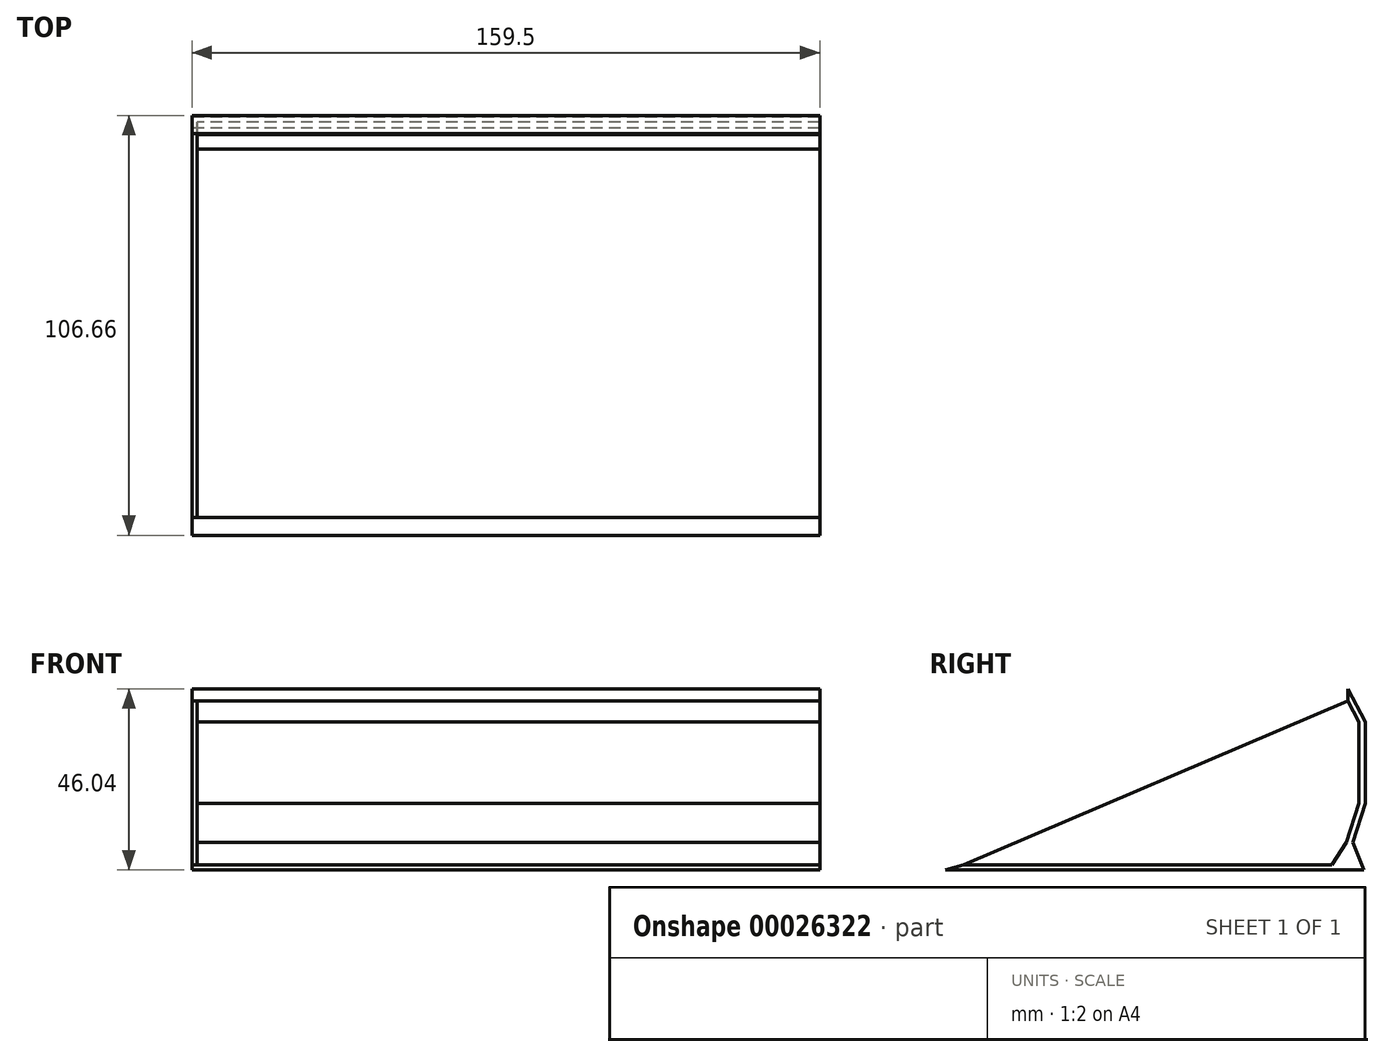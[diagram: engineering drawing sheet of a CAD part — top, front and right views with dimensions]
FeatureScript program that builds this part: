
annotation { "Feature Type Name" : "Feature", "Feature Type Description" : "" }
export const myFeature = defineFeature(function(context is Context, id is Id, definition is map)
    precondition{}
    {
        {
            var Q0;
            Q0=qCreatedBy(makeId("Right.planeOp"),FACE);
            var sketch = newSketch(context, id + "F0", { "sketchPlane" : qUnion([Q0])});
            skLineSegment(sketch, "E0", {"start": v(-60.67, 0) * mm, "end": v(38.43, 0) * mm});
            skLineSegment(sketch, "E1", {"start": v(38.43, 0) * mm, "end": v(42.78, 7) * mm});
            skLineSegment(sketch, "E2", {"start": v(42.78, 7) * mm, "end": v(45.62, 0) * mm});
            skLineSegment(sketch, "E3", {"start": v(45.62, 0) * mm, "end": v(38.43, 0) * mm});
            skLineSegment(sketch, "E4", {"start": v(42.78, 7) * mm, "end": v(46, 16.86) * mm});
            skLineSegment(sketch, "E5", {"start": v(46, 16.86) * mm, "end": v(46, 37.6) * mm});
            skLineSegment(sketch, "E6", {"start": v(46, 37.6) * mm, "end": v(41.44, 46.04) * mm});
            skLineSegment(sketch, "E7", {"start": v(41.44, 46.04) * mm, "end": v(41.44, 42.99) * mm});
            skLineSegment(sketch, "E8", {"start": v(41.44, 42.99) * mm, "end": v(44.35, 37.6) * mm});
            skLineSegment(sketch, "E9", {"start": v(44.35, 37.6) * mm, "end": v(44.35, 16.86) * mm});
            skLineSegment(sketch, "E10", {"start": v(44.35, 16.86) * mm, "end": v(41.18, 7) * mm});
            skLineSegment(sketch, "E11", {"start": v(41.18, 7) * mm, "end": v(37.5, 1.35) * mm});
            skLineSegment(sketch, "E12", {"start": v(37.5, 1.35) * mm, "end": v(-56.16, 1.35) * mm});
            skLineSegment(sketch, "E13", {"start": v(-56.16, 1.35) * mm, "end": v(-60.67, 0) * mm});
            skLineSegment(sketch, "E14", {"start": v(41.44, 42.99) * mm, "end": v(-56.16, 1.35) * mm});
            skSolve(sketch);
        }
        {
            var Q0;
            Q0=makeQuery(id+"F0.imprint","IMPRINT",FACE,{"disambiguationData":[TD([[makeQuery(id+"F0.imprint","IMPRINT",EDGE,{"derivedFrom":sQuery(id+"F0.wireOp",EDGE,"E0")}),1.0]])]});
            var Q1;
            Q1=makeQuery(id+"F0.imprint","IMPRINT",FACE,{"disambiguationData":[TD([[makeQuery(id+"F0.imprint","IMPRINT",EDGE,{"derivedFrom":sQuery(id+"F0.wireOp",EDGE,"E1")}),-1.0]])]});
            var Q2;
            Q2 = qSketchRegion(id + "F2", true);
            extrude(context, id + "F1", {"entities" : qUnion([Q0, Q1, Q2]), "depth" : 158.22 * mm});
        }
        {
            var Q0;
            Q0=qCreatedBy(makeId("Right.planeOp"),FACE);
            var sketch = newSketch(context, id + "F2", { "sketchPlane" : qUnion([Q0])});
            skSolve(sketch);
        }
        {
            var Q0;
            Q0=makeQuery(id+"F0.imprint","IMPRINT",FACE,{"disambiguationData":[TD([[makeQuery(id+"F0.imprint","IMPRINT",EDGE,{"derivedFrom":sQuery(id+"F0.wireOp",EDGE,"E8")}),-1.0]])]});
            var Q1;
            Q1=makeQuery(id+"F0.imprint","IMPRINT",FACE,{"disambiguationData":[TD([[makeQuery(id+"F0.imprint","IMPRINT",EDGE,{"derivedFrom":sQuery(id+"F0.wireOp",EDGE,"E1")}),-1.0]])]});
            var Q2;
            Q2=makeQuery(id+"F0.imprint","IMPRINT",FACE,{"disambiguationData":[TD([[makeQuery(id+"F0.imprint","IMPRINT",EDGE,{"derivedFrom":sQuery(id+"F0.wireOp",EDGE,"E0")}),1.0]])]});
            extrude(context, id + "F3", {"entities" : qUnion([Q0, Q1, Q2]), "operationType" : NewBodyOperationType.ADD, "oppositeDirection" : true, "depth" : 1.28 * mm});
        }
    });
